# Revit family: Настенный блок VRF системы
name_source: partatom
category: Mechanical Equipment
revit_build: Autodesk Revit 2016 (Build: 20150506_1715(x64)
units: mm (PartAtom-declared; Revit-internal decimal feet)

## family parameters
Cut with Voids When Loaded = No
Host = Face
Part Type = Normal
Room Calculation Point = No
Round Connector Dimension = Use Diameter
Shared = No

## types (5) — shared parameters
Default Elevation = 1219.2 mm  [stored 4 ft]
Высота = 315 mm  [stored 1.03346 ft]
Глубина = 230 mm  [stored 0.754593 ft]
Диаметр дренажного шлага = 16 mm  [stored 0.0524934 ft]
Наименование = Настенный блок VRF-системы
Номинал предохранителя = 10 A
Производитель = Electrolux
Таблица модель = Модель
Таблица наименование = Наименование
Таблица параметров = Таблица параметров
Таблица расход воздуха = Расход воздуха
Таблица уровень звукового давления = Уровень звукового давления
Таблица электропитание = Электропитание
Фаза = 1
Частота сети = 50 Hz
Эл. питание(коннектор) = 220 V
Электропитание, (В) = 220

## per-type parameters (varying)
| type | Артикул | Вес | Диаметр газовой трубы | Диаметр жидкостной трубы | Максимальная потребляемая мощность | Расход воздуха, (м.куб/ч) | Теплопроизводительность | Уровень звукового давления, (Дб(А)) | Холодопроизводительность | Ширина |
| ESVMW-SF-22S | 1100943 | 13.50 kg | 12.7 mm  [stored 0.0416667 ft] | 6.35 mm  [stored 0.0208333 ft] | 0.03 kW | 360-420-540 | 2.50 kW | 33-31-26 | 2.20 kW | 960 mm  [stored 3.14961 ft] |
| ESVMW-SF-28S | 1100944 | 13.50 kg | 12.7 mm  [stored 0.0416667 ft] | 6.35 mm  [stored 0.0208333 ft] | 0.03 kW | 650-600-550 | 3.20 kW | 33-31-26 | 2.80 kW | 960 mm  [stored 3.14961 ft] |
| ESVMW-SF-40S | 1100946 | 13.50 kg | 12.7 mm  [stored 0.0416667 ft] | 6.35 mm  [stored 0.0208333 ft] | 0.04 kW | 720-630-570 | 4.80 kW | 35-33-31 | 4.00 kW | 960 mm  [stored 3.14961 ft] |
| ESVMW-SF-56S | 1100947 | 16.00 kg | 15.88 mm  [stored 0.0520997 ft] | 9.53 mm | 0.05 kW | 770-700-620 | 6.30 kW | 38-36-34 | 5.60 kW | 1120 mm  [stored 3.67454 ft] |
| ESVMW-SF-71S | 1100948 | 16.00 kg | 15.88 mm  [stored 0.0520997 ft] | 9.53 mm | 0.05 kW | 820-770-710 | 8.00 kW | 40-37-34 | 7.10 kW | 1120 mm  [stored 3.67454 ft] |

note: column(s) folded — value = type name in every type: Модель

note: [stored X ft] marks values corroborated as IEEE doubles in the binary element streams (Revit-internal decimal feet)
